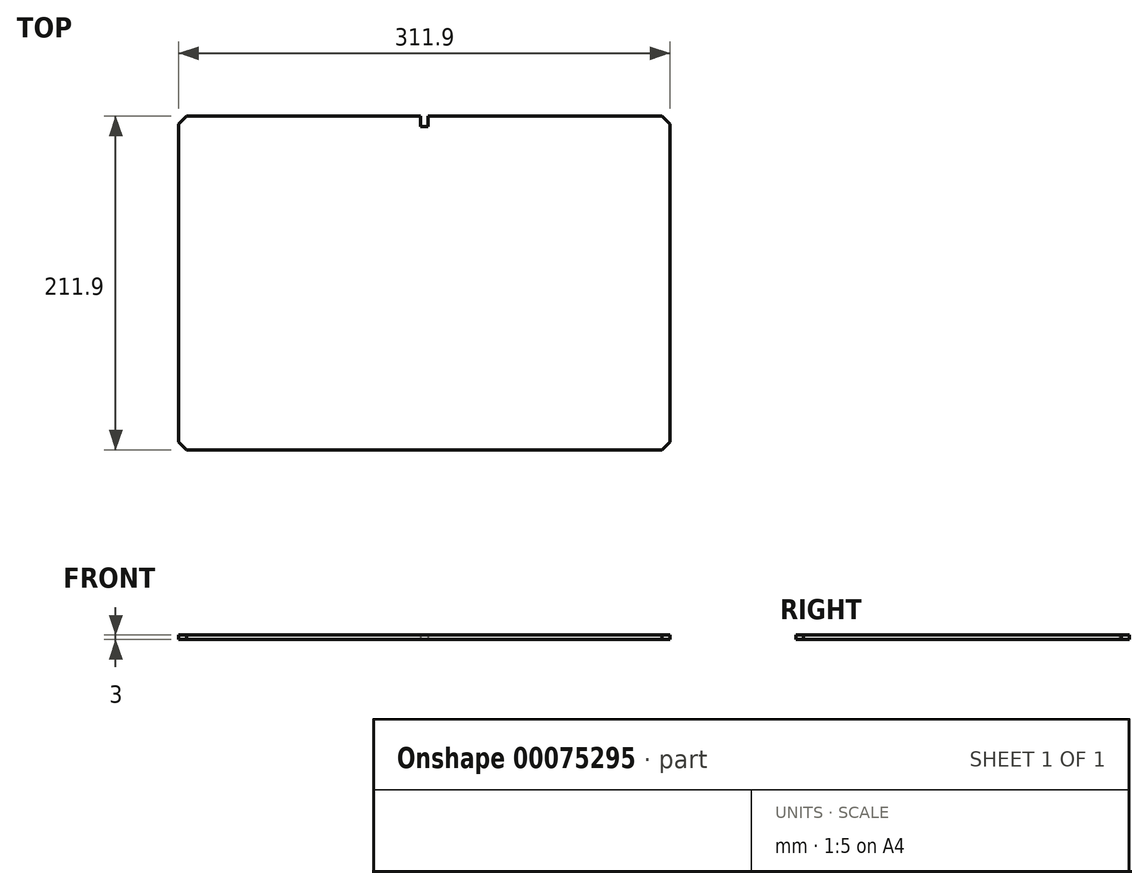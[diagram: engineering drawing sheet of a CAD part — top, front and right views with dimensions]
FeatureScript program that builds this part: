
annotation { "Feature Type Name" : "Feature", "Feature Type Description" : "" }
export const myFeature = defineFeature(function(context is Context, id is Id, definition is map)
    precondition{}
    {
        {
            var Q0;
            Q0=qCreatedBy(makeId("Top.planeOp"),FACE);
            var sketch = newSketch(context, id + "F0", { "sketchPlane" : qUnion([Q0])});
            skLineSegment(sketch, "E0.bottom", {"start": v(552.22, 210.45) * mm, "end": v(861.22, 210.45) * mm, "construction": true});
            skLineSegment(sketch, "E0.top", {"start": v(552.22, 1.45) * mm, "end": v(861.22, 1.45) * mm, "construction": true});
            skLineSegment(sketch, "E0.left", {"start": v(552.22, 210.45) * mm, "end": v(552.22, 1.45) * mm, "construction": true});
            skLineSegment(sketch, "E0.right", {"start": v(861.22, 210.45) * mm, "end": v(861.22, 1.45) * mm, "construction": true});
            skCircle(sketch, "E1", {"center": v(552.22, 210.45) * mm, "radius": 1.45 * mm, "construction": true});
            skCircle(sketch, "E2", {"center": v(861.22, 210.45) * mm, "radius": 1.45 * mm, "construction": true});
            skCircle(sketch, "E3", {"center": v(861.22, 1.45) * mm, "radius": 1.45 * mm, "construction": true});
            skCircle(sketch, "E4", {"center": v(552.22, 1.45) * mm, "radius": 1.45 * mm, "construction": true});
            skLineSegment(sketch, "E5", {"start": v(550.77, 206.9) * mm, "end": v(555.77, 211.9) * mm});
            skLineSegment(sketch, "E6", {"start": v(857.67, 211.9) * mm, "end": v(862.67, 206.9) * mm});
            skLineSegment(sketch, "E7", {"start": v(862.67, 5) * mm, "end": v(857.67, 0) * mm});
            skLineSegment(sketch, "E8", {"start": v(550.77, 5) * mm, "end": v(555.77, 0) * mm});
            skLineSegment(sketch, "E9", {"start": v(555.77, 0) * mm, "end": v(857.67, 0) * mm});
            skLineSegment(sketch, "E10", {"start": v(862.67, 5) * mm, "end": v(862.67, 206.9) * mm});
            skLineSegment(sketch, "E11", {"start": v(857.67, 211.9) * mm, "end": v(709.22, 211.9) * mm});
            skLineSegment(sketch, "E12", {"start": v(550.77, 206.9) * mm, "end": v(550.77, 5) * mm});
            skLineSegment(sketch, "E13", {"start": v(706.72, 210.45) * mm, "end": v(706.72, 205.45) * mm, "construction": true});
            skLineSegment(sketch, "E14", {"start": v(704.22, 205.45) * mm, "end": v(704.22, 211.9) * mm});
            skLineSegment(sketch, "E15", {"start": v(704.22, 205.45) * mm, "end": v(709.22, 205.45) * mm});
            skLineSegment(sketch, "E16", {"start": v(709.22, 205.45) * mm, "end": v(709.22, 211.9) * mm});
            skLineSegment(sketch, "E17.trimOffspring", {"start": v(704.22, 211.9) * mm, "end": v(555.77, 211.9) * mm});
            skSolve(sketch);
        }
        {
            var Q0;
            Q0 = qSketchRegion(id + "F0", true);
            extrude(context, id + "F1", {"entities" : qUnion([Q0]), "depth" : 3 * mm});
        }
    });
